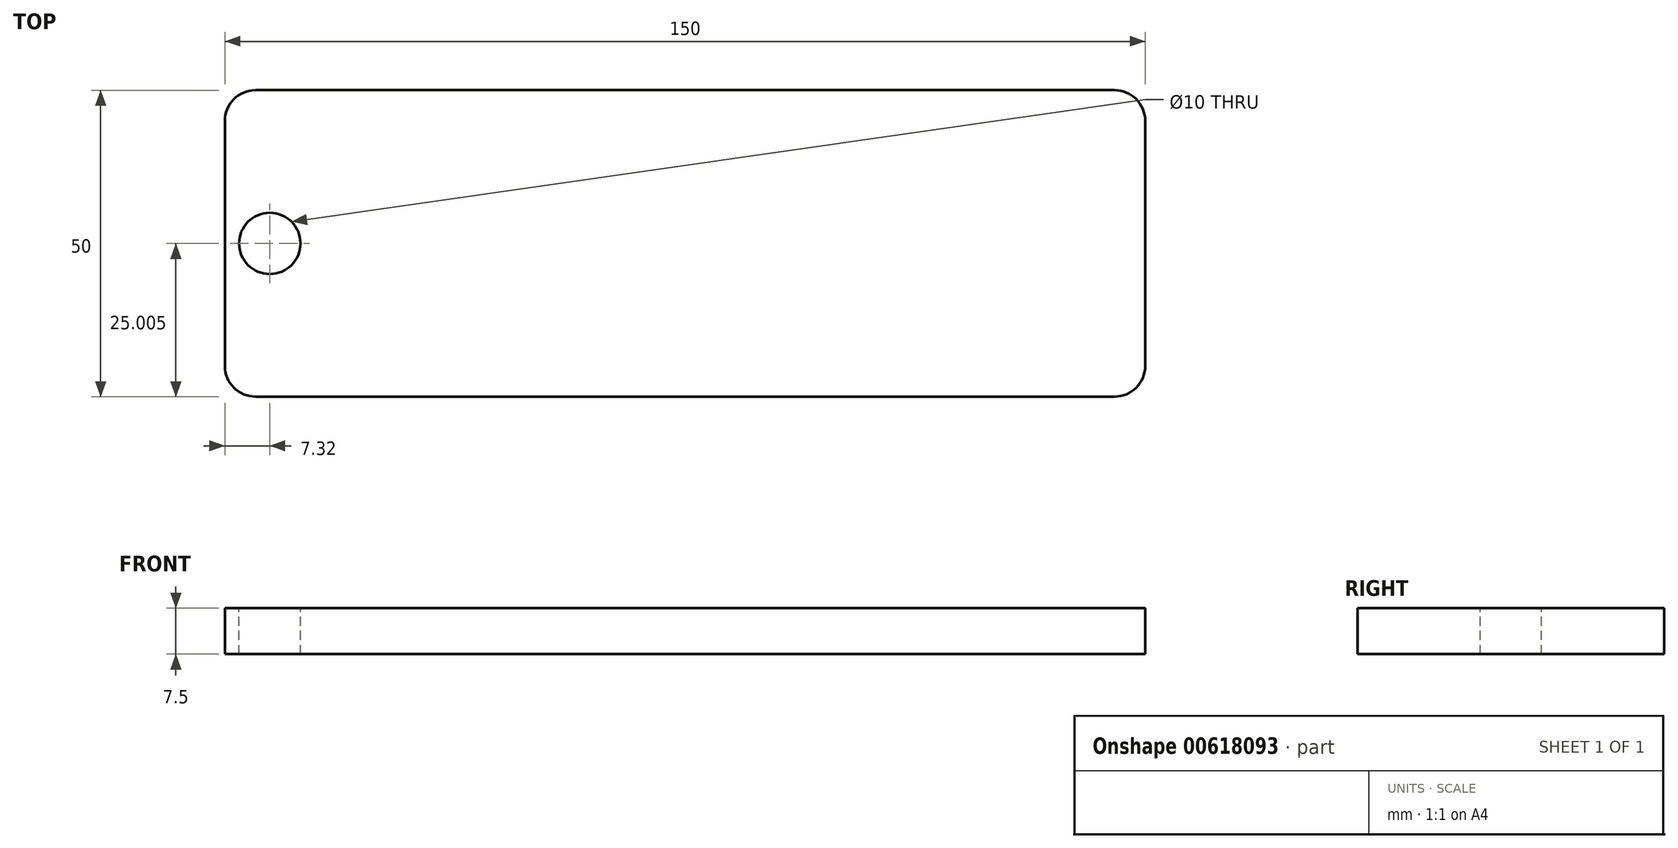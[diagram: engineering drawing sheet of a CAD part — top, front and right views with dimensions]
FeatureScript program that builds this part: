
annotation { "Feature Type Name" : "Feature", "Feature Type Description" : "" }
export const myFeature = defineFeature(function(context is Context, id is Id, definition is map)
    precondition{}
    {
        {
            var Q0;
            Q0=qCreatedBy(makeId("Top.planeOp"),FACE);
            var sketch = newSketch(context, id + "F0", { "sketchPlane" : qUnion([Q0])});
            skLineSegment(sketch, "E0.bottom", {"start": v(-7.32, 48.46) * mm, "end": v(142.68, 48.46) * mm});
            skLineSegment(sketch, "E0.top", {"start": v(-7.32, -1.54) * mm, "end": v(142.68, -1.54) * mm});
            skLineSegment(sketch, "E0.left", {"start": v(-7.32, 48.46) * mm, "end": v(-7.32, -1.54) * mm});
            skLineSegment(sketch, "E0.right", {"start": v(142.68, 48.46) * mm, "end": v(142.68, -1.54) * mm});
            skSolve(sketch);
        }
        {
            var Q0;
            Q0=makeQuery(id+"F0.imprint","IMPRINT",FACE,{"disambiguationData":[TD([[makeQuery(id+"F0.imprint","IMPRINT",EDGE,{"derivedFrom":sQuery(id+"F0.wireOp",EDGE,"E0.bottom")}),-1.0]])]});
            extrude(context, id + "F1", {"entities" : qUnion([Q0]), "depth" : 7.5 * mm, "offsetDistance" : 25 * mm});
        }
        {
            var Q0;
            Q0=makeQuery(id+"F1.opExtrude","SWEPT_EDGE",EDGE,{"disambiguationData":[OSD([sQuery(id+"F0.wireOp",EDGE,"E0.top"),sQuery(id+"F0.wireOp",EDGE,"E0.left")])]});
            fillet(context, id + "F2", {"entities" : qUnion([Q0]), "radius" : 5 * mm, "tangentPropagation" : true, "allowEdgeOverflow" : false});
        }
        {
            var Q0;
            Q0=makeQuery(id+"F1.opExtrude","SWEPT_EDGE",EDGE,{"disambiguationData":[OSD([sQuery(id+"F0.wireOp",EDGE,"E0.bottom"),sQuery(id+"F0.wireOp",EDGE,"E0.left")])]});
            fillet(context, id + "F3", {"entities" : qUnion([Q0]), "radius" : 5 * mm, "tangentPropagation" : true, "allowEdgeOverflow" : false});
        }
        {
            var Q0;
            Q0=makeQuery(id+"F1.opExtrude","SWEPT_EDGE",EDGE,{"disambiguationData":[OSD([sQuery(id+"F0.wireOp",EDGE,"E0.top"),sQuery(id+"F0.wireOp",EDGE,"E0.right")])]});
            fillet(context, id + "F4", {"entities" : qUnion([Q0]), "radius" : 5 * mm, "tangentPropagation" : true, "allowEdgeOverflow" : false});
        }
        {
            var Q0;
            Q0=makeQuery(id+"F1.opExtrude","SWEPT_EDGE",EDGE,{"disambiguationData":[OSD([sQuery(id+"F0.wireOp",EDGE,"E0.bottom"),sQuery(id+"F0.wireOp",EDGE,"E0.right")])]});
            fillet(context, id + "F5", {"entities" : qUnion([Q0]), "radius" : 5 * mm, "tangentPropagation" : true, "allowEdgeOverflow" : false});
        }
        {
            var Q0;
            Q0=makeQuery(id+"F1.opExtrude","CAP_FACE",FACE,{"disambiguationData":[OSD([sQuery(id+"F0.wireOp",EDGE,"E0.bottom"),sQuery(id+"F0.wireOp",EDGE,"E0.top"),sQuery(id+"F0.wireOp",EDGE,"E0.left"),sQuery(id+"F0.wireOp",EDGE,"E0.right")])],"isStart":false});
            var sketch = newSketch(context, id + "F6", { "sketchPlane" : qUnion([Q0])});
            skLineSegment(sketch, "E1", {"start": v(0, 48.46) * mm, "end": v(0, 23.46) * mm});
            skCircle(sketch, "E2", {"center": v(0, 23.46) * mm, "radius": 5 * mm});
            skSolve(sketch);
        }
        {
            var Q0;
            Q0 = qSketchRegion(id + "F6", true);
            extrude(context, id + "F7", {"entities" : qUnion([Q0]), "operationType" : NewBodyOperationType.REMOVE, "oppositeDirection" : true, "depth" : 25 * mm, "offsetDistance" : 25 * mm});
        }
    });
